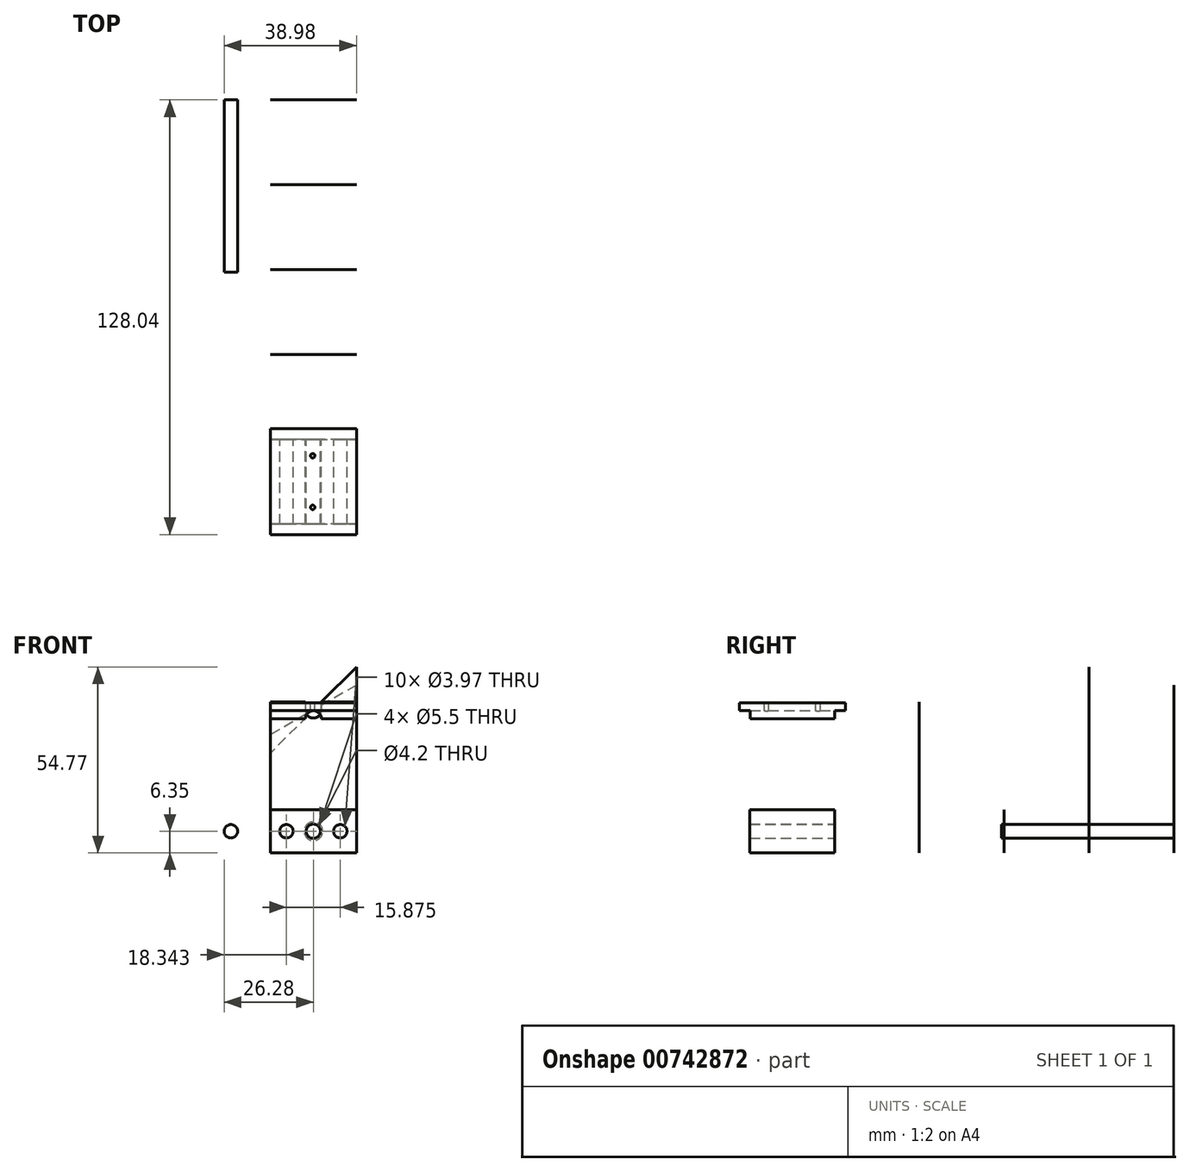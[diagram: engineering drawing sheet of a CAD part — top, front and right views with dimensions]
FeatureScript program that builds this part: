
annotation { "Feature Type Name" : "Feature", "Feature Type Description" : "" }
export const myFeature = defineFeature(function(context is Context, id is Id, definition is map)
    precondition{}
    {
        {
            var Q0;
            Q0=qCreatedBy(makeId("Front.planeOp"),FACE);
            cPlane(context, id + "F0", {"entities" : qUnion([Q0]), "cplaneType" : CPlaneType.OFFSET, "offset" : 25 * mm, "oppositeDirection" : true, "width" : 150 * mm, "height" : 150 * mm});
        }
        {
            var Q0;
            Q0=qCreatedBy(makeId("Front.planeOp"),FACE);
            cPlane(context, id + "F1", {"entities" : qUnion([Q0]), "cplaneType" : CPlaneType.OFFSET, "offset" : 50 * mm, "oppositeDirection" : true, "width" : 150 * mm, "height" : 150 * mm});
        }
        {
            var Q0;
            Q0=qCreatedBy(makeId("Front.planeOp"),FACE);
            cPlane(context, id + "F2", {"entities" : qUnion([Q0]), "cplaneType" : CPlaneType.OFFSET, "offset" : 75 * mm, "oppositeDirection" : true, "width" : 150 * mm, "height" : 150 * mm});
        }
        {
            var Q0;
            Q0=qCreatedBy(makeId("Front.planeOp"),FACE);
            cPlane(context, id + "F3", {"entities" : qUnion([Q0]), "cplaneType" : CPlaneType.OFFSET, "offset" : 100 * mm, "oppositeDirection" : true, "width" : 150 * mm, "height" : 150 * mm});
        }
        {
            var Q0;
            Q0=qCreatedBy(makeId("Front.planeOp"),FACE);
            var sketch = newSketch(context, id + "F4", { "sketchPlane" : qUnion([Q0])});
            skLineSegment(sketch, "E0.bottom", {"start": v(0, 0) * mm, "end": v(25.4, 0) * mm});
            skLineSegment(sketch, "E0.top", {"start": v(0, 12.7) * mm, "end": v(25.4, 12.7) * mm});
            skLineSegment(sketch, "E0.left", {"start": v(0, 0) * mm, "end": v(0, 12.7) * mm});
            skLineSegment(sketch, "E0.right", {"start": v(25.4, 0) * mm, "end": v(25.4, 12.7) * mm});
            skLineSegment(sketch, "E1", {"start": v(0, 6.35) * mm, "end": v(25.4, 6.35) * mm, "construction": true});
            skLineSegment(sketch, "E2", {"start": v(12.7, 0) * mm, "end": v(12.7, 12.7) * mm, "construction": true});
            skCircle(sketch, "E3", {"center": v(12.7, 6.35) * mm, "radius": 2.1 * mm});
            skLineSegment(sketch, "E4", {"start": v(4.76, 12.7) * mm, "end": v(4.76, 0) * mm, "construction": true});
            skLineSegment(sketch, "E5", {"start": v(20.64, 12.7) * mm, "end": v(20.64, 0) * mm, "construction": true});
            skCircle(sketch, "E6", {"center": v(4.76, 6.35) * mm, "radius": 1.98 * mm});
            skCircle(sketch, "E7", {"center": v(20.64, 6.35) * mm, "radius": 1.98 * mm});
            skSolve(sketch);
        }
        {
            var Q0;
            Q0=makeQuery(id+"F4.imprint","IMPRINT",FACE,{"disambiguationData":[TD([[makeQuery(id+"F4.imprint","IMPRINT",EDGE,{"derivedFrom":sQuery(id+"F4.wireOp",EDGE,"E0.bottom")}),1.0]])]});
            extrude(context, id + "F5", {"entities" : qUnion([Q0]), "depth" : (31.2 - 6.24) * mm, "offsetDistance" : 25 * mm});
        }
        {
            var Q0;
            Q0=qCreatedBy(id+"F0.planeOp",FACE);
            var sketch = newSketch(context, id + "F6", { "sketchPlane" : qUnion([Q0])});
            skLineSegment(sketch, "E8.bottom", {"start": v(0, 0) * mm, "end": v(25.4, 0) * mm});
            skLineSegment(sketch, "E8.top", {"start": v(0, 42.07) * mm, "end": v(25.4, 42.07) * mm, "construction": true});
            skLineSegment(sketch, "E8.left", {"start": v(0, 0) * mm, "end": v(0, 44.45) * mm});
            skLineSegment(sketch, "E8.right", {"start": v(25.4, 0) * mm, "end": v(25.4, 44.45) * mm});
            skArc(sketch, "E9", {"start": v(10.32, 42.07) * mm, "mid": v(12.7, 39.69) * mm, "end": v(15.08, 42.07) * mm});
            skCircle(sketch, "E10.0", {"center": v(20.64, 6.35) * mm, "radius": 1.98 * mm});
            skCircle(sketch, "E11.0", {"center": v(4.76, 6.35) * mm, "radius": 1.98 * mm});
            skLineSegment(sketch, "E12", {"start": v(25.4, 44.45) * mm, "end": v(15.08, 44.45) * mm});
            skLineSegment(sketch, "E13", {"start": v(15.08, 44.45) * mm, "end": v(15.08, 42.07) * mm});
            skLineSegment(sketch, "E14", {"start": v(10.32, 44.45) * mm, "end": v(10.32, 42.07) * mm});
            skLineSegment(sketch, "E15.trimOffspring", {"start": v(10.32, 44.45) * mm, "end": v(0, 44.45) * mm});
            skCircle(sketch, "E16", {"center": v(12.7, 6.35) * mm, "radius": 2.75 * mm});
            skSolve(sketch);
        }
        {
            var Q0;
            Q0=makeQuery(id+"F6.imprint","IMPRINT",FACE,{"disambiguationData":[TD([[makeQuery(id+"F6.imprint","IMPRINT",EDGE,{"derivedFrom":sQuery(id+"F6.wireOp",EDGE,"E8.bottom")}),1.0]])]});
            extrude(context, id + "F7", {"entities" : qUnion([Q0]), "oppositeDirection" : true, "depth" : 1 / 203.2 * mm, "offsetDistance" : 25 * mm});
        }
        {
            var Q0;
            Q0=qCreatedBy(id+"F1.planeOp",FACE);
            var sketch = newSketch(context, id + "F8", { "sketchPlane" : qUnion([Q0])});
            skLineSegment(sketch, "E17.0.0", {"start": v(0, 12.7) * mm, "end": v(25.4, 12.7) * mm});
            skLineSegment(sketch, "E17.0.1", {"start": v(25.4, 12.7) * mm, "end": v(25.4, 0) * mm});
            skLineSegment(sketch, "E17.0.2", {"start": v(25.4, 0) * mm, "end": v(0, 0) * mm});
            skLineSegment(sketch, "E17.0.3", {"start": v(0, 0) * mm, "end": v(0, 12.7) * mm});
            skCircle(sketch, "E18.0", {"center": v(20.64, 6.35) * mm, "radius": 1.98 * mm});
            skCircle(sketch, "E19.0", {"center": v(4.76, 6.35) * mm, "radius": 1.98 * mm});
            skCircle(sketch, "E20.0", {"center": v(12.7, 6.35) * mm, "radius": 2.75 * mm});
            skSolve(sketch);
        }
        {
            var Q0;
            Q0=makeQuery(id+"F8.imprint","IMPRINT",FACE,{"disambiguationData":[TD([[makeQuery(id+"F8.imprint","IMPRINT",EDGE,{"derivedFrom":sQuery(id+"F8.wireOp",EDGE,"E17.0.0")}),-1.0]])]});
            extrude(context, id + "F9", {"entities" : qUnion([Q0]), "oppositeDirection" : true, "depth" : 3 / 406.4 * mm, "offsetDistance" : 25 * mm});
        }
        {
            var Q0;
            Q0=qCreatedBy(id+"F2.planeOp",FACE);
            var sketch = newSketch(context, id + "F10", { "sketchPlane" : qUnion([Q0])});
            skArc(sketch, "E21.0.1", {"start": v(11.02, 40.38) * mm, "mid": v(13.61, 39.87) * mm, "end": v(15.08, 42.07) * mm});
            skLineSegment(sketch, "E21.0.2", {"start": v(15.08, 42.07) * mm, "end": v(15.08, 44.45) * mm});
            skLineSegment(sketch, "E21.0.4", {"start": v(25.4, 54.77) * mm, "end": v(25.4, 0) * mm});
            skLineSegment(sketch, "E21.0.5", {"start": v(25.4, 0) * mm, "end": v(0, 0) * mm});
            skLineSegment(sketch, "E21.0.6", {"start": v(0, 0) * mm, "end": v(0, 29.37) * mm});
            skCircle(sketch, "E22.0", {"center": v(20.64, 6.35) * mm, "radius": 1.98 * mm});
            skCircle(sketch, "E23.0", {"center": v(4.76, 6.35) * mm, "radius": 1.98 * mm});
            skLineSegment(sketch, "E24", {"start": v(25.4, 54.77) * mm, "end": v(15.08, 44.45) * mm});
            skLineSegment(sketch, "E25", {"start": v(11.02, 40.38) * mm, "end": v(0, 29.37) * mm});
            skCircle(sketch, "E26.0", {"center": v(12.7, 6.35) * mm, "radius": 2.75 * mm});
            skSolve(sketch);
        }
        {
            var Q0;
            Q0=makeQuery(id+"F10.imprint","IMPRINT",FACE,{"disambiguationData":[TD([[makeQuery(id+"F10.imprint","IMPRINT",EDGE,{"derivedFrom":sQuery(id+"F10.wireOp",EDGE,"E21.0.1")}),-1.0]])]});
            extrude(context, id + "F11", {"entities" : qUnion([Q0]), "oppositeDirection" : true, "depth" : 3 / 406.4 * mm, "offsetDistance" : 25 * mm});
        }
        {
            var Q0;
            Q0=qCreatedBy(id+"F3.planeOp",FACE);
            var sketch = newSketch(context, id + "F12", { "sketchPlane" : qUnion([Q0])});
            skLineSegment(sketch, "E27.0.0", {"start": v(0, 0) * mm, "end": v(0, 34.74) * mm});
            skArc(sketch, "E27.0.2", {"start": v(10.64, 40.88) * mm, "mid": v(13.32, 39.77) * mm, "end": v(15.08, 42.07) * mm});
            skLineSegment(sketch, "E27.0.3", {"start": v(15.08, 42.07) * mm, "end": v(15.08, 43.44) * mm});
            skLineSegment(sketch, "E27.0.5", {"start": v(25.4, 49.4) * mm, "end": v(25.4, 0) * mm});
            skLineSegment(sketch, "E27.0.6", {"start": v(25.4, 0) * mm, "end": v(0, 0) * mm});
            skCircle(sketch, "E28.0", {"center": v(20.64, 6.35) * mm, "radius": 1.98 * mm});
            skCircle(sketch, "E29.0", {"center": v(4.76, 6.35) * mm, "radius": 1.98 * mm});
            skLineSegment(sketch, "E30", {"start": v(25.4, 49.4) * mm, "end": v(15.08, 43.44) * mm});
            skLineSegment(sketch, "E31", {"start": v(10.64, 40.88) * mm, "end": v(0, 34.74) * mm});
            skCircle(sketch, "E32.0", {"center": v(12.7, 6.35) * mm, "radius": 2.75 * mm});
            skSolve(sketch);
        }
        {
            var Q0;
            Q0=makeQuery(id+"F12.imprint","IMPRINT",FACE,{"disambiguationData":[TD([[makeQuery(id+"F12.imprint","IMPRINT",EDGE,{"derivedFrom":sQuery(id+"F12.wireOp",EDGE,"E27.0.0")}),-1.0]])]});
            extrude(context, id + "F13", {"entities" : qUnion([Q0]), "oppositeDirection" : true, "depth" : 3 / 406.4 * mm, "offsetDistance" : 25 * mm});
        }
        {
            var Q0;
            Q0=qCreatedBy(id+"F3.planeOp",FACE);
            var sketch = newSketch(context, id + "F14", { "sketchPlane" : qUnion([Q0])});
            skCircle(sketch, "E33", {"center": v(-11.6, 6.35) * mm, "radius": 1.98 * mm});
            skSolve(sketch);
        }
        {
            var Q0;
            Q0=makeQuery(id+"F14.imprint","IMPRINT",FACE,{"disambiguationData":[TD([[makeQuery(id+"F14.imprint","IMPRINT",EDGE,{"derivedFrom":sQuery(id+"F14.wireOp",EDGE,"E33")}),1.0]])]});
            extrude(context, id + "F15", {"entities" : qUnion([Q0]), "depth" : 50.8 * mm, "offsetDistance" : 25 * mm});
        }
        {
            var Q0;
            Q0=qCreatedBy(makeId("Right.planeOp"),FACE);
            var sketch = newSketch(context, id + "F16", { "sketchPlane" : qUnion([Q0])});
            skLineSegment(sketch, "E34.bottom", {"start": v(-28.03, 44.23) * mm, "end": v(3.18, 44.23) * mm});
            skLineSegment(sketch, "E34.top", {"start": v(-24.85, 39.46) * mm, "end": v(0, 39.46) * mm});
            skLineSegment(sketch, "E34.left", {"start": v(-28.03, 44.23) * mm, "end": v(-28.03, 41.84) * mm});
            skLineSegment(sketch, "E34.right", {"start": v(3.18, 44.23) * mm, "end": v(3.18, 41.84) * mm});
            skLineSegment(sketch, "E35.bottom", {"start": v(0, 41.84) * mm, "end": v(3.18, 41.84) * mm});
            skLineSegment(sketch, "E35.left", {"start": v(0, 41.84) * mm, "end": v(0, 39.46) * mm});
            skPoint(sketch, "E36.firstSnap0", {"position": v(-28.03, 41.84) * mm});
            skLineSegment(sketch, "E36.bottom", {"start": v(-24.85, 41.84) * mm, "end": v(-28.03, 41.84) * mm});
            skLineSegment(sketch, "E36.left", {"start": v(-24.85, 41.84) * mm, "end": v(-24.85, 39.46) * mm});
            skSolve(sketch);
        }
        {
            var Q0;
            Q0=makeQuery(id+"F16.imprint","IMPRINT",FACE,{"disambiguationData":[TD([[makeQuery(id+"F16.imprint","IMPRINT",EDGE,{"derivedFrom":sQuery(id+"F16.wireOp",EDGE,"E34.bottom")}),-1.0]])]});
            extrude(context, id + "F17", {"entities" : qUnion([Q0]), "depth" : 25.4 * mm, "offsetDistance" : 25 * mm});
        }
        {
            var Q0;
            Q0=qCreatedBy(makeId("Front.planeOp"),FACE);
            var sketch = newSketch(context, id + "F18", { "sketchPlane" : qUnion([Q0])});
            skLineSegment(sketch, "E37.0", {"start": v(25.4, 41.84) * mm, "end": v(0, 41.84) * mm});
            skLineSegment(sketch, "E38", {"start": v(12.7, 41.84) * mm, "end": v(12.7, 35.65) * mm, "construction": true});
            skLineSegment(sketch, "E39.0", {"start": v(25.4, 39.46) * mm, "end": v(0, 39.46) * mm});
            skCircle(sketch, "E40", {"center": v(12.7, 39.46) * mm, "radius": 2.38 * mm});
            skSolve(sketch);
        }
        {
            var Q0;
            {var subQ0=sQuery(id+"F18.wireOp",EDGE,"E40");var subQ1=sQuery(id+"F18.wireOp",EDGE,"E39.0");var subQ2=makeQuery(id+"F18.imprint","INTERSECT",VERTEX,{"disambiguationData":[OD(0.0)],"derivedFrom":[subQ1,subQ0]});Q0=makeQuery(id+"F18.imprint","IMPRINT",FACE,{"disambiguationData":[TD([[makeQuery(id+"F18.imprint","IMPRINT",EDGE,{"disambiguationData":[TD([[subQ2,1.0]])],"derivedFrom":subQ1}),-1.0]])]});}
            var Q1;
            Q1=makeQuery(id+"F17.opExtrude","CAP_VERTEX",VERTEX,{"disambiguationData":[OSD([sQuery(id+"F16.wireOp",EDGE,"E34.top"),sQuery(id+"F16.wireOp",EDGE,"E36.left")])],"isStart":false});
            extrude(context, id + "F19", {"entities" : qUnion([Q0]), "operationType" : NewBodyOperationType.REMOVE, "endBound" : BoundingType.UP_TO_VERTEX, "depth" : 50 * mm, "endBoundEntityVertex" : qUnion([Q1]), "offsetDistance" : 25 * mm});
        }
        {
            var Q0;
            Q0=makeQuery(id+"F17.opExtrude","SWEPT_FACE",FACE,{"disambiguationData":[OSD([sQuery(id+"F16.wireOp",EDGE,"E34.bottom")])]});
            cPlane(context, id + "F20", {"entities" : qUnion([Q0]), "cplaneType" : CPlaneType.OFFSET, "offset" : 25 * mm, "width" : 150 * mm, "height" : 150 * mm});
        }
        {
            var Q0;
            Q0=qCreatedBy(id+"F20.planeOp",FACE);
            var sketch = newSketch(context, id + "F21", { "sketchPlane" : qUnion([Q0])});
            skLineSegment(sketch, "E41.0", {"start": v(25.4, -28.03) * mm, "end": v(0, -28.03) * mm});
            skLineSegment(sketch, "E42.0", {"start": v(25.4, 3.17) * mm, "end": v(0, 3.17) * mm});
            skLineSegment(sketch, "E43", {"start": v(12.7, -28.03) * mm, "end": v(12.7, 3.17) * mm, "construction": true});
            skLineSegment(sketch, "E44", {"start": v(0, -20.03) * mm, "end": v(25, -20.03) * mm, "construction": true});
            skLineSegment(sketch, "E45", {"start": v(0, -4.83) * mm, "end": v(25, -4.82) * mm, "construction": true});
            skCircle(sketch, "E46", {"center": v(12.5, -20.03) * mm, "radius": 0.65 * mm});
            skCircle(sketch, "E47", {"center": v(12.5, -4.82) * mm, "radius": 0.65 * mm});
            skSolve(sketch);
        }
        {
            var Q0;
            Q0=makeQuery(id+"F21.imprint","IMPRINT",FACE,{"disambiguationData":[TD([[makeQuery(id+"F21.imprint","IMPRINT",EDGE,{"derivedFrom":sQuery(id+"F21.wireOp",EDGE,"E46")}),1.0]])]});
            var Q1;
            Q1=makeQuery(id+"F21.imprint","IMPRINT",FACE,{"disambiguationData":[TD([[makeQuery(id+"F21.imprint","IMPRINT",EDGE,{"derivedFrom":sQuery(id+"F21.wireOp",EDGE,"E47")}),1.0]])]});
            var Q2;
            Q2=sQuery(id+"F21.wireOp",EDGE,"E46");
            var Q3;
            Q3=sQuery(id+"F21.wireOp",EDGE,"E47");
            var Q4;
            Q4=makeQuery(id+"F19.boolean.opBoolean","COPY",FACE,{"derivedFrom":makeQuery(id+"F19.opExtrude","SWEPT_FACE",FACE,{"disambiguationData":[OSD([sQuery(id+"F18.wireOp",EDGE,"E40")])]})});
            extrude(context, id + "F22", {"entities" : qUnion([Q0, Q1]), "operationType" : NewBodyOperationType.REMOVE, "surfaceEntities" : qUnion([Q2, Q3]), "endBound" : BoundingType.UP_TO_SURFACE, "oppositeDirection" : true, "depth" : 25 * mm, "endBoundEntityFace" : qUnion([Q4]), "offsetDistance" : 25 * mm});
        }
    });
